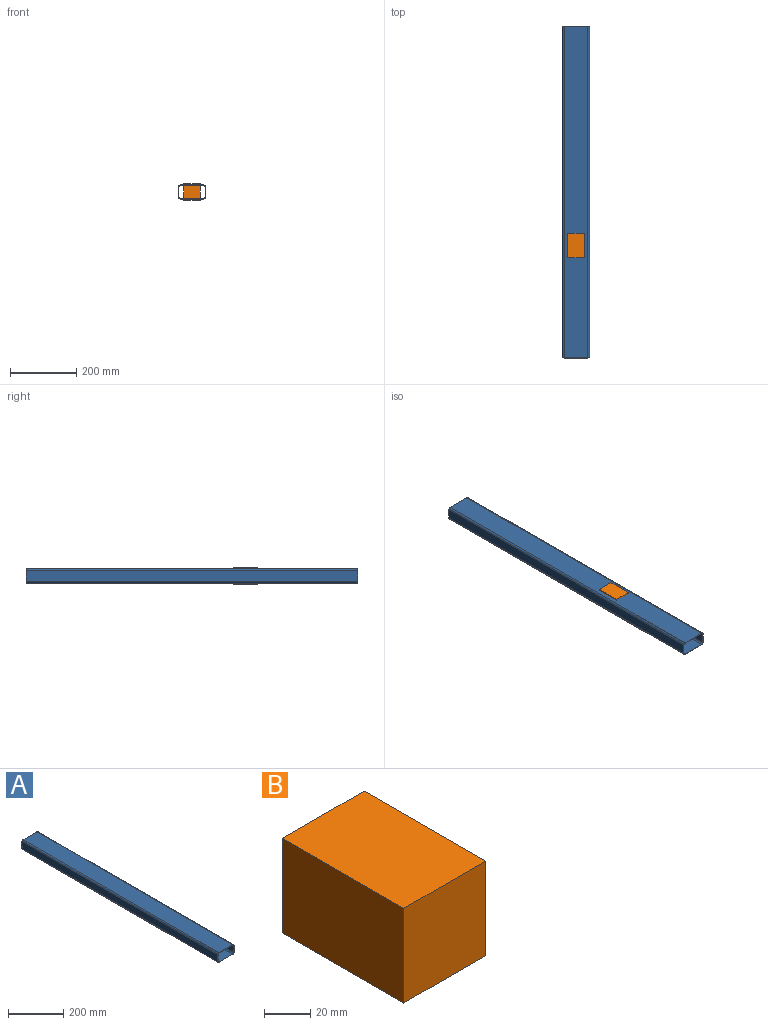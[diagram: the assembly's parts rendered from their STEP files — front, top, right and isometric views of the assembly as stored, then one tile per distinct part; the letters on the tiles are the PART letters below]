
ASSEMBLY  parts=2 mates=1
PART A: 18 faces, bbox 82.2x1000x42.2 mm
  f0: plane 1000x32.2mm, normal (1,0,0), area 32200mm2, adj f1,f15,f16,f17
  f1: cylinder r=5mm len=1000mm, axis (0,1,0), area 7854mm2, adj f0,f2,f16,f17
  f2: plane 1000x72.2mm, normal (0,0,1), area 72200mm2, adj f1,f3,f16,f17
  f3: cylinder r=5mm len=1000mm, axis (0,1,0), area 7854mm2, adj f2,f4,f16,f17
  f4: plane 1000x32.2mm, normal (-1,0,0), area 32200mm2, adj f3,f5,f16,f17
  f5: cylinder r=5mm len=1000mm, axis (0,1,0), area 7854mm2, adj f4,f6,f16,f17
  f6: plane 1000x72.2mm, normal (0,0,-1), area 72200mm2, adj f5,f15,f16,f17
  f7: cylinder r=5mm len=1000mm, axis (0,1,0), area 7854mm2, adj f8,f14,f16,f17
  f8: plane 1000x30mm, normal (-1,0,0), area 30000mm2, adj f7,f9,f16,f17
  f9: cylinder r=5mm len=1000mm, axis (0,1,0), area 7854mm2, adj f8,f10,f16,f17
  f10: plane 1000x70mm, normal (0,0,1), area 70000mm2, adj f9,f11,f16,f17
  f11: cylinder r=5mm len=1000mm, axis (0,1,0), area 7854mm2, adj f10,f12,f16,f17
  f12: plane 1000x30mm, normal (1,0,0), area 30000mm2, adj f11,f13,f16,f17
  f13: cylinder r=5mm len=1000mm, axis (0,1,0), area 7854mm2, adj f12,f14,f16,f17
  f14: plane 1000x70mm, normal (0,0,-1), area 70000mm2, adj f7,f13,f16,f17
  f15: cylinder r=5mm len=1000mm, axis (0,1,0), area 7854mm2, adj f0,f6,f16,f17
  f16: plane 82.2x42.2mm, normal (0,-1,0), area 268.8mm2, adj f0,f1,f2,f3,f4,f5,f6,f7
  f17: plane 82.2x42.2mm, normal (0,1,0), area 268.8mm2, adj f0,f1,f2,f3,f4,f5,f6,f7
PART B: 6 faces, bbox 50x74.1x50 mm
  f0: plane 74.1x50mm, normal (0,0,1), area 3705mm2, adj f1,f3,f4,f5
  f1: plane 74.1x50mm, normal (-1,0,0), area 3705mm2, adj f0,f2,f4,f5
  f2: plane 74.1x50mm, normal (0,0,-1), area 3705mm2, adj f1,f3,f4,f5
  f3: plane 74.1x50mm, normal (1,0,0), area 3705mm2, adj f0,f2,f4,f5
  f4: plane 50x50mm, normal (0,-1,0), area 2500mm2, adj f0,f1,f2,f3
  f5: plane 50x50mm, normal (0,1,0), area 2500mm2, adj f0,f1,f2,f3
PLACE A rot(axis=(-1,0,0),180deg) t=(0,0,0)mm
PLACE B rot(axis=(1,0,0),180deg) t=(0,339.05,0)mm
MATE slider A.f17 <-> B.f5  axis (0,-1,0) through (0,0,0)mm
